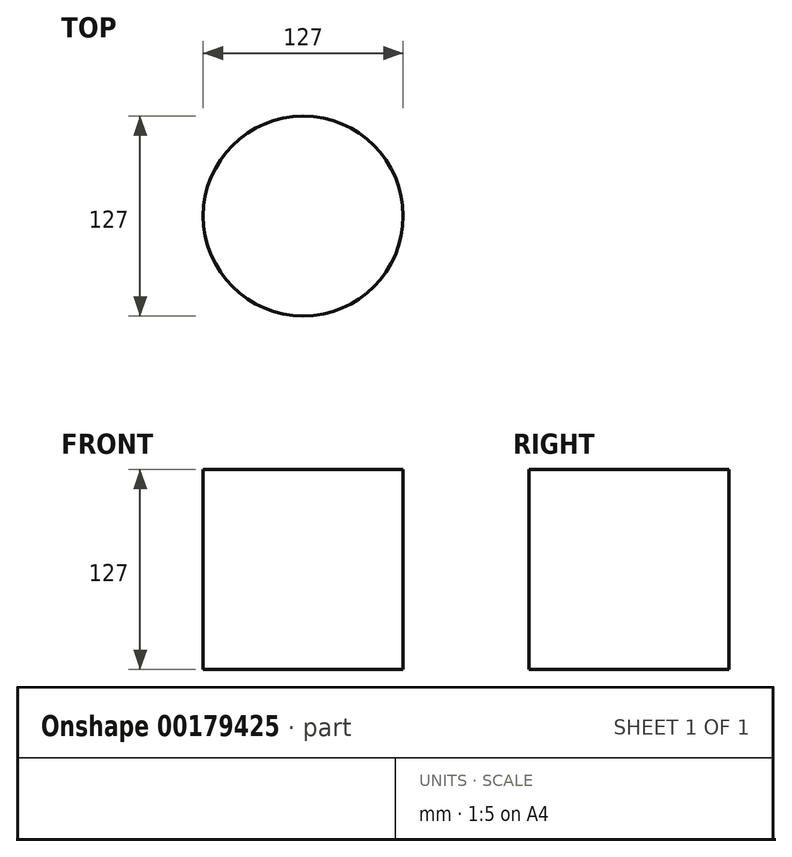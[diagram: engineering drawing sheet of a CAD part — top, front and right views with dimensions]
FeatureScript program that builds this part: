
annotation { "Feature Type Name" : "Feature", "Feature Type Description" : "" }
export const myFeature = defineFeature(function(context is Context, id is Id, definition is map)
    precondition{}
    {
        {
            var Q0;
            Q0=qCreatedBy(makeId("Top.planeOp"),FACE);
            var sketch = newSketch(context, id + "F0", { "sketchPlane" : qUnion([Q0])});
            skCircle(sketch, "E0", {"center": v(0, 0) * mm, "radius": 63.5 * mm});
            skSolve(sketch);
        }
        {
            var Q0;
            Q0 = qSketchRegion(id + "F0", true);
            extrude(context, id + "F1", {"entities" : qUnion([Q0]), "depth" : 127 * mm});
        }
    });
